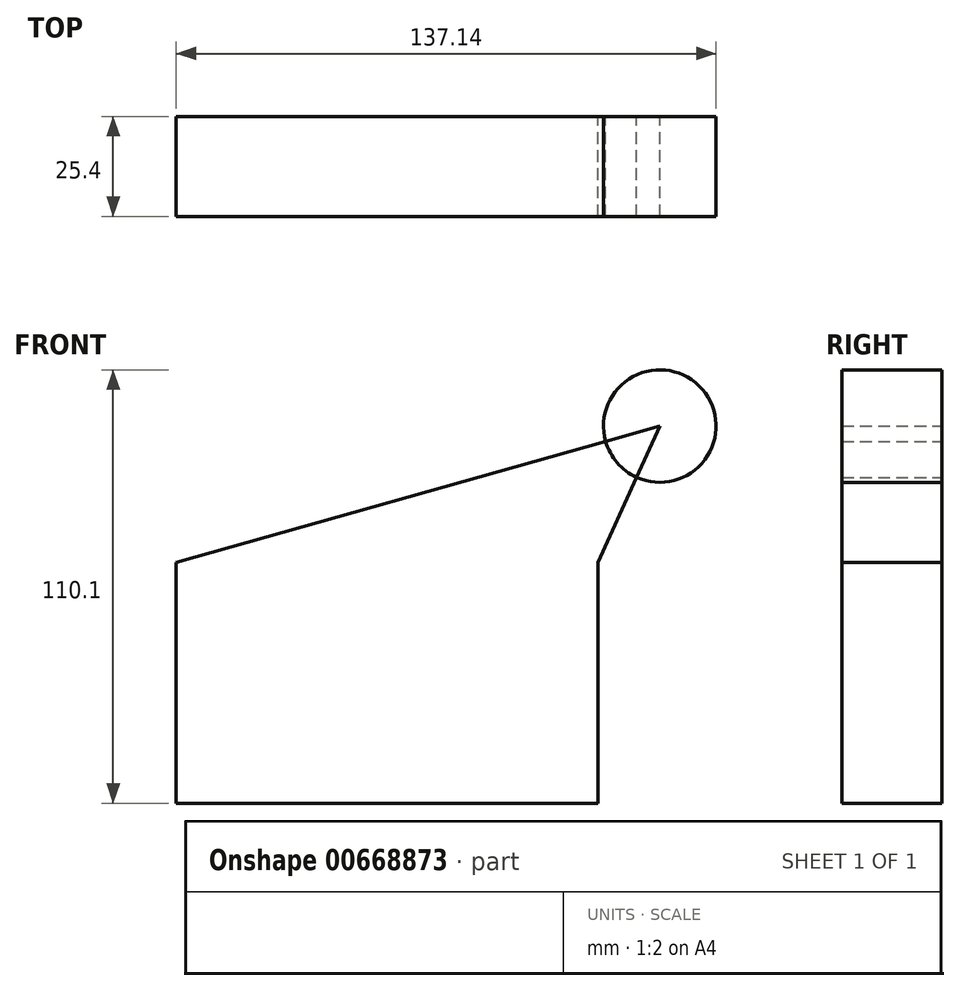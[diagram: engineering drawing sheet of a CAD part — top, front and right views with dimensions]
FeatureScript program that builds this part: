
annotation { "Feature Type Name" : "Feature", "Feature Type Description" : "" }
export const myFeature = defineFeature(function(context is Context, id is Id, definition is map)
    precondition{}
    {
        {
            var Q0;
            Q0=qCreatedBy(makeId("Front.planeOp"),FACE);
            var sketch = newSketch(context, id + "F0", { "sketchPlane" : qUnion([Q0])});
            skLineSegment(sketch, "E0.bottom", {"start": v(53.58, -30.55) * mm, "end": v(-53.58, -30.55) * mm});
            skLineSegment(sketch, "E0.top", {"start": v(53.58, 30.55) * mm, "end": v(-53.58, 30.55) * mm});
            skLineSegment(sketch, "E0.left", {"start": v(53.58, -30.55) * mm, "end": v(53.58, 30.55) * mm});
            skLineSegment(sketch, "E0.right", {"start": v(-53.58, -30.55) * mm, "end": v(-53.58, 30.55) * mm});
            skPoint(sketch, "E0.middle", {"position": v(0, 0) * mm});
            skCircle(sketch, "E1", {"center": v(69.27, 65.27) * mm, "radius": 14.29 * mm});
            skLineSegment(sketch, "E2", {"start": v(53.58, 30.55) * mm, "end": v(69.27, 65.27) * mm});
            skLineSegment(sketch, "E3", {"start": v(-53.58, 30.55) * mm, "end": v(69.27, 65.27) * mm});
            skSolve(sketch);
        }
        {
            var Q0;
            {var subQ0=sQuery(id+"F0.wireOp",EDGE,"E2");var subQ1=sQuery(id+"F0.wireOp",EDGE,"E1");var subQ2=makeQuery(id+"F0.imprint","INTERSECT",VERTEX,{"derivedFrom":[subQ1,subQ0]});Q0=makeQuery(id+"F0.imprint","IMPRINT",FACE,{"disambiguationData":[TD([[makeQuery(id+"F0.imprint","IMPRINT",EDGE,{"disambiguationData":[TD([[subQ2,-1.0]])],"derivedFrom":subQ1}),1.0]])]});}
            var Q1;
            Q1=makeQuery(id+"F0.imprint","IMPRINT",FACE,{"disambiguationData":[TD([[makeQuery(id+"F0.imprint","IMPRINT",EDGE,{"derivedFrom":sQuery(id+"F0.wireOp",EDGE,"E0.bottom")}),-1.0]])]});
            var Q2;
            {var subQ0=sQuery(id+"F0.wireOp",EDGE,"E0.top");Q2=makeQuery(id+"F0.imprint","IMPRINT",FACE,{"disambiguationData":[TD([[makeQuery(id+"F0.imprint","IMPRINT",EDGE,{"derivedFrom":subQ0}),-1.0]])]});}
            extrude(context, id + "F1", {"entities" : qUnion([Q0, Q1, Q2]), "depth" : 25.4 * mm, "offsetDistance" : 25.4 * mm});
        }
    });
